# Revit family: 64140101
name_source: partatom
category: Plumbing Fixtures
revit_build: Autodesk Revit 2016 (Build: 20150220_1215(x64)
units: mm (PartAtom-declared; Revit-internal decimal feet)

## family parameters
Always vertical = Yes
Cut with Voids When Loaded = No
OmniClass Number = 23.45.55.00
OmniClass Title = Sanitary Faucets, Wastes
Part Type = Normal
Room Calculation Point = No
Round Connector Dimension = Use Diameter
Shared = No
Work Plane-Based = No

## types (1)
- 64140101 Shower faucet
    2D/3D/BIM Files URL = http://static.hansa.com
    Advanced Features = DZR brass
    AssetType = Fixed
    BIMObjectName = 64140101
    BodyMaterial = Brass
    Brand = Hansa
    Catalog Drawing URL = http://static.hansa.com
    Category = Bathroom, shower
    Class = Thermostatic
    CloseOffRating = 0
    Color = Chrome
    Connection = Eccentric unions
    ConvergoRefNr = 0087-1809-0070-FI
    Customs Code = 84818011
    DN Size = DN15
    Dimension Drawing URL = http://static.hansa.com
    DurationUnit = Year
    EAN Number = 4015474277274
    FDV Document URL = http://www.hansa.com
    FaucetMainMaterial = Brass
    Features = Thermostatic
    Finish = Polished
    Flow Drawing URL = http://static.hansa.com
    Flow Rate At 300kPa = 0.3 L/s
    FlowCoefficient = 0
    Group = Shower faucets
    IfcExportAs = IfcValveType
    IfcExportType = FAUCET
    Installation Type = Wall-mounted
    Installation Width = cc150 ± 15 mm
    Installation and Maintenance = http://static.hansa.com
    Lever Handle = Flow control handle
    ManufacterURL = http://www.hansa.com
    Manufacturer = Hansa
    ManufacturerName = Hansa
    Market = BEL;CZE;ESP;FRA;INT;ITA;NLD;SVK
    Material = Brass
    Mechanical Parts = Litter filter(s), ceramic head part
    Model = 64140101 Shower faucet
    ModelReference = 64140101
    NBSDescription = Water supply fittings for baths
    NBSReference = 45-35-70/315
    Name = 64140101 Shower faucet
    Name_en = 64140101 Shower faucet
    NominalDepth = 110 mm  [stored 0.360892 ft]
    NominalHeight = 73 mm
    NominalWidth = 285 mm
    Package Weight = 2.62 kg
    Package external Dimensions = 285 x 155 x 75
    Product Code = 64140101
    Product Datasheet = http://www.hansa.com
    Product Family = HANSALANO
    Product Image URL = http://static.hansa.com
    Product URL = http://static.hansa.com
    Revision = 2
    Safety Sales Arguments = Our thermostats offer maximum safety with protection against scalding.
    Shape = Sculptured
    Size = 285x110x75 mm
    Spare Parts = http://static.hansa.com
    Technology Sales Arguments = Suitable for instantaneous water heaters (shower above 20 kW or bathtub)
    Temperature = Thermostatic temperature control, thermostatic safety stop at 38°C
    Uniclass2 = Pr_40_30_96_81
    Uniclass2015Description = Shower thermostatic water supply sets
    Uniclass2015Reference = Pr_40_20_87_81
    Version = 2
    VersionDate = 01/01/2019
    WarrantyDescription = http://warranty.hansa.com
    WarrantyDurationUnit = Year

note: [stored X ft] marks values corroborated as IEEE doubles in the binary element streams (Revit-internal decimal feet)

## geometry (parser evidence)
native form markers: Sweep x6
no freeform markers — native parametric forms only
